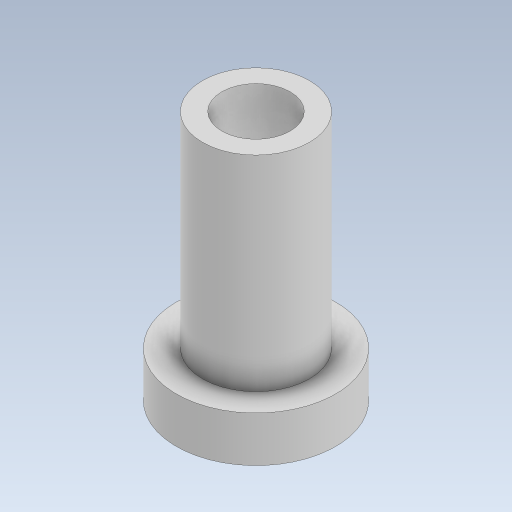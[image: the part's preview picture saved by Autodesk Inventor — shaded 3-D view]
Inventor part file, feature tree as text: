
AUTODESK INVENTOR PART (.ipt)
format: ipt  version: 2023.5 (Build 275446000, 446)  size: 277,504 bytes
history: native  units: mm
features: extrude x3, sketch x2
ambient origin geometry x8: Origin, YZ Plane, XZ Plane, XY Plane, X Axis, Y Axis, Z Axis, Center Point
bodies: Solid1 (feature_tree)
feature tree (5):
  sketch  "Sketch1"  dims[d0=7.0mm d1=4.7mm]
  extrude  "Extrusion1"  Depth=7.0mm
  extrude  "Extrusion2"  Depth=2.0mm TaperAngle=0.0deg
  extrude  "Extrusion3"  Depth=7.0mm
  sketch  "Sketch2"  dims[d2=11.0mm d3=0.0mm d4=2.0mm d5=0.0mm d6=3.0mm d7=7.0mm d8=0.0mm]
